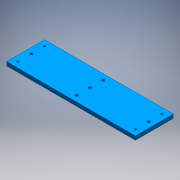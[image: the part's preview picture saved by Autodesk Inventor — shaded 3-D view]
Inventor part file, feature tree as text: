
AUTODESK INVENTOR PART (.ipt)
format: ipt  version: 2016 (Build 200138000, 138)  size: 140,800 bytes
history: native  units: mm
features: sketch x3, hole x2, mirror x2, extrude x1
ambient origin geometry x8: Origin, YZ Plane, XZ Plane, XY Plane, X Axis, Y Axis, Z Axis, Center Point
bodies: Solid1 (feature_tree)
feature tree (8):
  extrude  "baseExtrusion"  Depth=340.0mm
  hole  "xyStiltpt1m6MountingHoles"  [1 undecoded]
  mirror  "Mirror2"
  mirror  "Mirror3"
  hole  "Hole3"  [1 undecoded]
  sketch  "Sketch1"  dims[d0=340.0mm d1=170.0mm]
  sketch  "Sketch2"  dims[d2=100.0mm d3=50.0mm]
  sketch  "Sketch4"  dims[d4=10.0mm d5=0.0mm d6=15.0mm d7=15.0mm d8=4.917mm d9=12.0mm d10=4.0mm d11=2.0mm d12=90.0deg d13=17.1mm d14=20.594885mm d24=15.0mm d25=15.0mm d26=15.0mm d27=15.0mm d28=6.6mm d29=12.0mm d30=18.0mm d31=4.8mm d32=90.0deg d33=17.1mm d34=20.594885mm]
note: 2 required parameter values undecoded (feature->parameter linkage not recoverable at this tier; creation-order binding heuristic only, values carry confidence <= 0.55)
